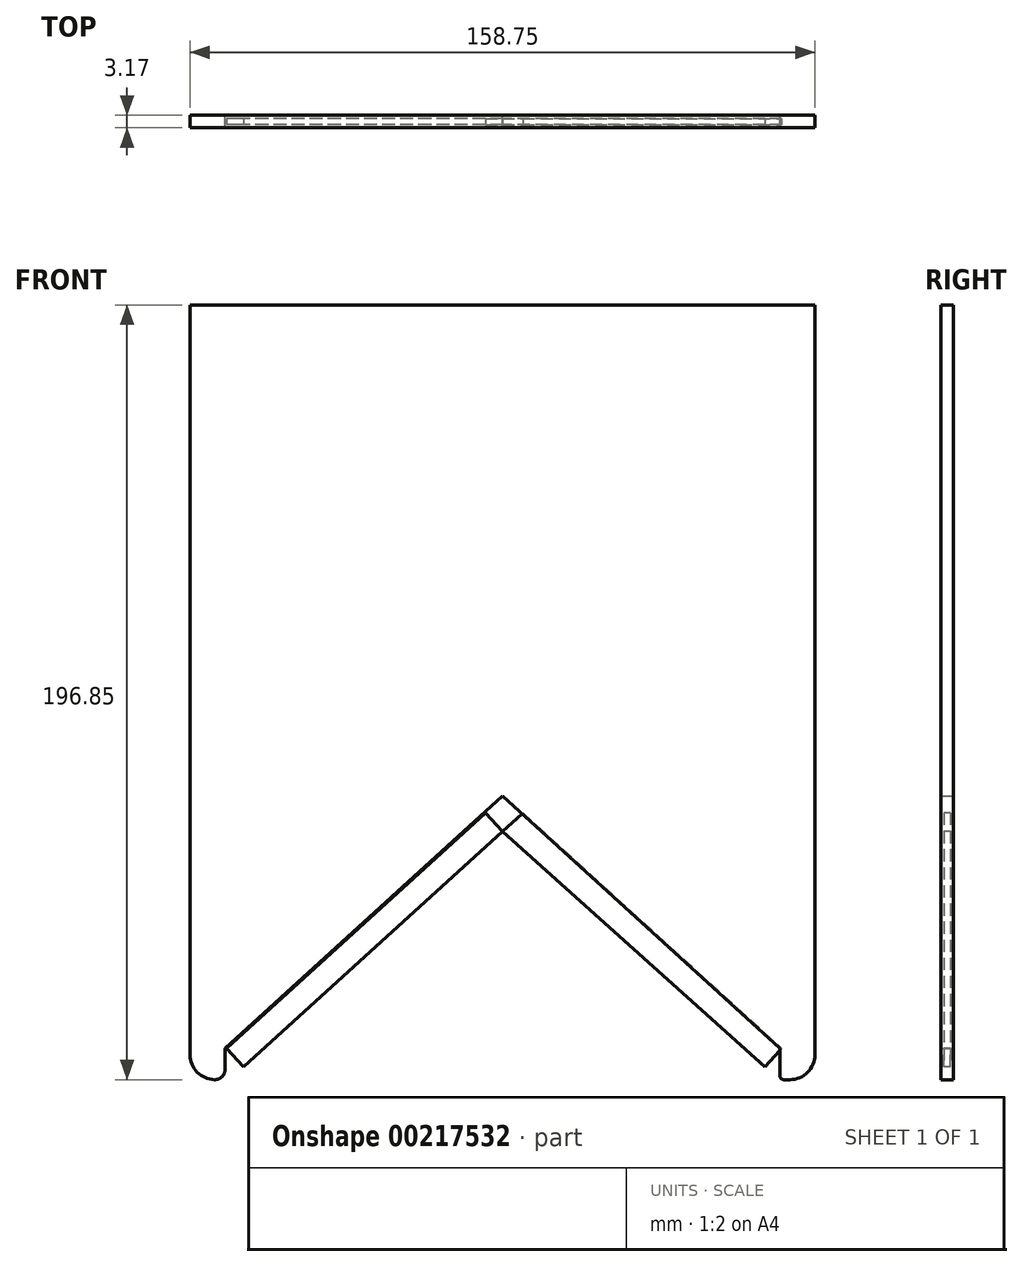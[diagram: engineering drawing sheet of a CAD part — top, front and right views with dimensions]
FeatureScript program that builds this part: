
annotation { "Feature Type Name" : "Feature", "Feature Type Description" : "" }
export const myFeature = defineFeature(function(context is Context, id is Id, definition is map)
    precondition{}
    {
        {
            var Q0;
            Q0=qCreatedBy(makeId("Front.planeOp"),FACE);
            var sketch = newSketch(context, id + "F0", { "sketchPlane" : qUnion([Q0])});
            skLineSegment(sketch, "E0.bottom", {"start": v(-84, 89.42) * mm, "end": v(74.76, 89.42) * mm});
            skLineSegment(sketch, "E0.top", {"start": v(-77.64, -107.43) * mm, "end": v(-74.47, -107.43) * mm});
            skLineSegment(sketch, "E0.left", {"start": v(-84, 89.42) * mm, "end": v(-84, -101.08) * mm});
            skLineSegment(sketch, "E0.right", {"start": v(74.76, 89.42) * mm, "end": v(74.76, -101.08) * mm});
            skLineSegment(sketch, "E1", {"start": v(-70.84, -104.14) * mm, "end": v(-4.62, -43.93) * mm});
            skPoint(sketch, "E1.endSnap0", {"position": v(-4.62, -107.43) * mm});
            skLineSegment(sketch, "E2", {"start": v(-4.62, -43.93) * mm, "end": v(61.6, -104.14) * mm});
            skLineSegment(sketch, "E3", {"start": v(-4.62, -43.93) * mm, "end": v(-9.32, -39.66) * mm});
            skLineSegment(sketch, "E4", {"start": v(-9.32, -39.66) * mm, "end": v(-75.1, -99.46) * mm});
            skLineSegment(sketch, "E5", {"start": v(-75.1, -99.46) * mm, "end": v(-70.84, -104.14) * mm});
            skLineSegment(sketch, "E6.MirrorCS", {"start": v(0.08, -39.66) * mm, "end": v(65.86, -99.46) * mm});
            skLineSegment(sketch, "E7.MirrorCS", {"start": v(-4.62, -43.93) * mm, "end": v(0.08, -39.66) * mm});
            skLineSegment(sketch, "E8.MirrorCS", {"start": v(65.86, -99.46) * mm, "end": v(61.6, -104.14) * mm});
            skLineSegment(sketch, "E9", {"start": v(-75.1, -99.46) * mm, "end": v(-75.1, -104.83) * mm});
            skLineSegment(sketch, "E10", {"start": v(-75.1, -107.43) * mm, "end": v(-75.1, -99.46) * mm});
            skLineSegment(sketch, "E11", {"start": v(-75.1, -99.46) * mm, "end": v(-4.62, -35.4) * mm});
            skLineSegment(sketch, "E12.MirrorCS", {"start": v(65.86, -99.46) * mm, "end": v(-4.62, -35.4) * mm});
            skLineSegment(sketch, "E13.MirrorCS", {"start": v(65.86, -106.44) * mm, "end": v(65.86, -99.46) * mm});
            skPoint(sketch, "E14.orphan", {"position": v(-74.47, -107.43) * mm});
            skLineSegment(sketch, "E15.trimOffspring", {"start": v(66.86, -107.43) * mm, "end": v(68.4, -107.43) * mm});
            skPoint(sketch, "E16.visualSharp", {"position": v(-84, -107.43) * mm});
            skArc(sketch, "E16.filletArc", {"start": v(-84, -101.08) * mm, "mid": v(-82.17, -105.54) * mm, "end": v(-77.74, -107.43) * mm});
            skArc(sketch, "E17.filletArc", {"start": v(-77.74, -107.43) * mm, "mid": v(-75.87, -106.69) * mm, "end": v(-75.1, -104.83) * mm});
            skPoint(sketch, "E18.visualSharp", {"position": v(74.76, -107.43) * mm});
            skArc(sketch, "E18.filletArc", {"start": v(68.4, -107.43) * mm, "mid": v(72.9, -105.57) * mm, "end": v(74.76, -101.08) * mm});
            skPoint(sketch, "E19.orphan", {"position": v(65.23, -107.43) * mm});
            skPoint(sketch, "E20.visualSharp", {"position": v(65.86, -107.43) * mm});
            skArc(sketch, "E20.filletArc", {"start": v(65.86, -106.44) * mm, "mid": v(66.15, -107.14) * mm, "end": v(66.86, -107.43) * mm});
            skSolve(sketch);
        }
        {
            var Q0;
            Q0=makeQuery(id+"F0.imprint","IMPRINT",FACE,{"disambiguationData":[TD([[makeQuery(id+"F0.imprint","IMPRINT",EDGE,{"derivedFrom":sQuery(id+"F0.wireOp",EDGE,"E0.bottom")}),-1.0]])]});
            extrude(context, id + "F1", {"entities" : qUnion([Q0]), "depth" : 3.17 * mm});
        }
        {
            var Q0;
            Q0=makeQuery(id+"F1.opExtrude","CAP_FACE",FACE,{"disambiguationData":[OSD([sQuery(id+"F0.wireOp",EDGE,"E0.bottom"),sQuery(id+"F0.wireOp",EDGE,"E0.left"),sQuery(id+"F0.wireOp",EDGE,"E0.right"),sQuery(id+"F0.wireOp",EDGE,"E10"),sQuery(id+"F0.wireOp",EDGE,"E11"),sQuery(id+"F0.wireOp",EDGE,"E12.MirrorCS"),sQuery(id+"F0.wireOp",EDGE,"E13.MirrorCS"),sQuery(id+"F0.wireOp",EDGE,"E15.trimOffspring"),sQuery(id+"F0.wireOp",EDGE,"E16.filletArc"),sQuery(id+"F0.wireOp",EDGE,"E17.filletArc"),sQuery(id+"F0.wireOp",EDGE,"E18.filletArc"),sQuery(id+"F0.wireOp",EDGE,"E20.filletArc")])],"isStart":false});
            var sketch = newSketch(context, id + "F2", { "sketchPlane" : qUnion([Q0])});
            skLineSegment(sketch, "E21", {"start": v(-9.32, -39.66) * mm, "end": v(-5.04, -44.36) * mm});
            skLineSegment(sketch, "E22", {"start": v(-5.04, -44.36) * mm, "end": v(-70.83, -104.16) * mm});
            skLineSegment(sketch, "E23", {"start": v(-70.83, -104.16) * mm, "end": v(-75.1, -99.46) * mm});
            skLineSegment(sketch, "E24", {"start": v(-75.1, -99.46) * mm, "end": v(-9.32, -39.66) * mm});
            skLineSegment(sketch, "E25", {"start": v(-5.04, -44.36) * mm, "end": v(0.12, -39.66) * mm});
            skLineSegment(sketch, "E26", {"start": v(0.12, -39.66) * mm, "end": v(65.86, -99.46) * mm});
            skLineSegment(sketch, "E27", {"start": v(65.86, -99.46) * mm, "end": v(61.6, -104.16) * mm});
            skLineSegment(sketch, "E28", {"start": v(61.6, -104.16) * mm, "end": v(-5.04, -44.36) * mm});
            skSolve(sketch);
        }
        {
            var Q0;
            Q0 = qSketchRegion(id + "F2", true);
            extrude(context, id + "F3", {"entities" : qUnion([Q0]), "oppositeDirection" : true, "depth" : 1.59 * mm});
        }
        {
            var Q0;
            Q0=makeQuery(id+"F3.opExtrude","SWEPT_BODY",BODY,{"disambiguationData":[OSD([sQuery(id+"F2.wireOp",EDGE,"E21"),sQuery(id+"F2.wireOp",EDGE,"E22"),sQuery(id+"F2.wireOp",EDGE,"E23"),sQuery(id+"F2.wireOp",EDGE,"E24")])]});
            var Q1;
            Q1=makeQuery(id+"F3.opExtrude","SWEPT_BODY",BODY,{"disambiguationData":[OSD([sQuery(id+"F2.wireOp",EDGE,"E25"),sQuery(id+"F2.wireOp",EDGE,"E26"),sQuery(id+"F2.wireOp",EDGE,"E27"),sQuery(id+"F2.wireOp",EDGE,"E28")])]});
            transform(context, id + "F4", {"entities" : qUnion([Q0, Q1]), "transformType" : TransformType.TRANSLATION_3D, "dx" : 0 * mm, "dy" : 0.8 * mm, "dz" : 0 * mm, "makeCopy" : false});
        }
        {
            var Q0;
            Q0=makeQuery(id+"F3.opExtrude","SWEPT_BODY",BODY,{"disambiguationData":[OSD([sQuery(id+"F2.wireOp",EDGE,"E21"),sQuery(id+"F2.wireOp",EDGE,"E22"),sQuery(id+"F2.wireOp",EDGE,"E23"),sQuery(id+"F2.wireOp",EDGE,"E24")])]});
            var Q1;
            Q1=makeQuery(id+"F3.opExtrude","SWEPT_BODY",BODY,{"disambiguationData":[OSD([sQuery(id+"F2.wireOp",EDGE,"E25"),sQuery(id+"F2.wireOp",EDGE,"E26"),sQuery(id+"F2.wireOp",EDGE,"E27"),sQuery(id+"F2.wireOp",EDGE,"E28")])]});
            transform(context, id + "F5", {"entities" : qUnion([Q0, Q1]), "transformType" : TransformType.TRANSLATION_3D, "dx" : 0.43 * mm, "dy" : 0 * mm, "dz" : 0 * mm, "makeCopy" : false});
        }
    });
